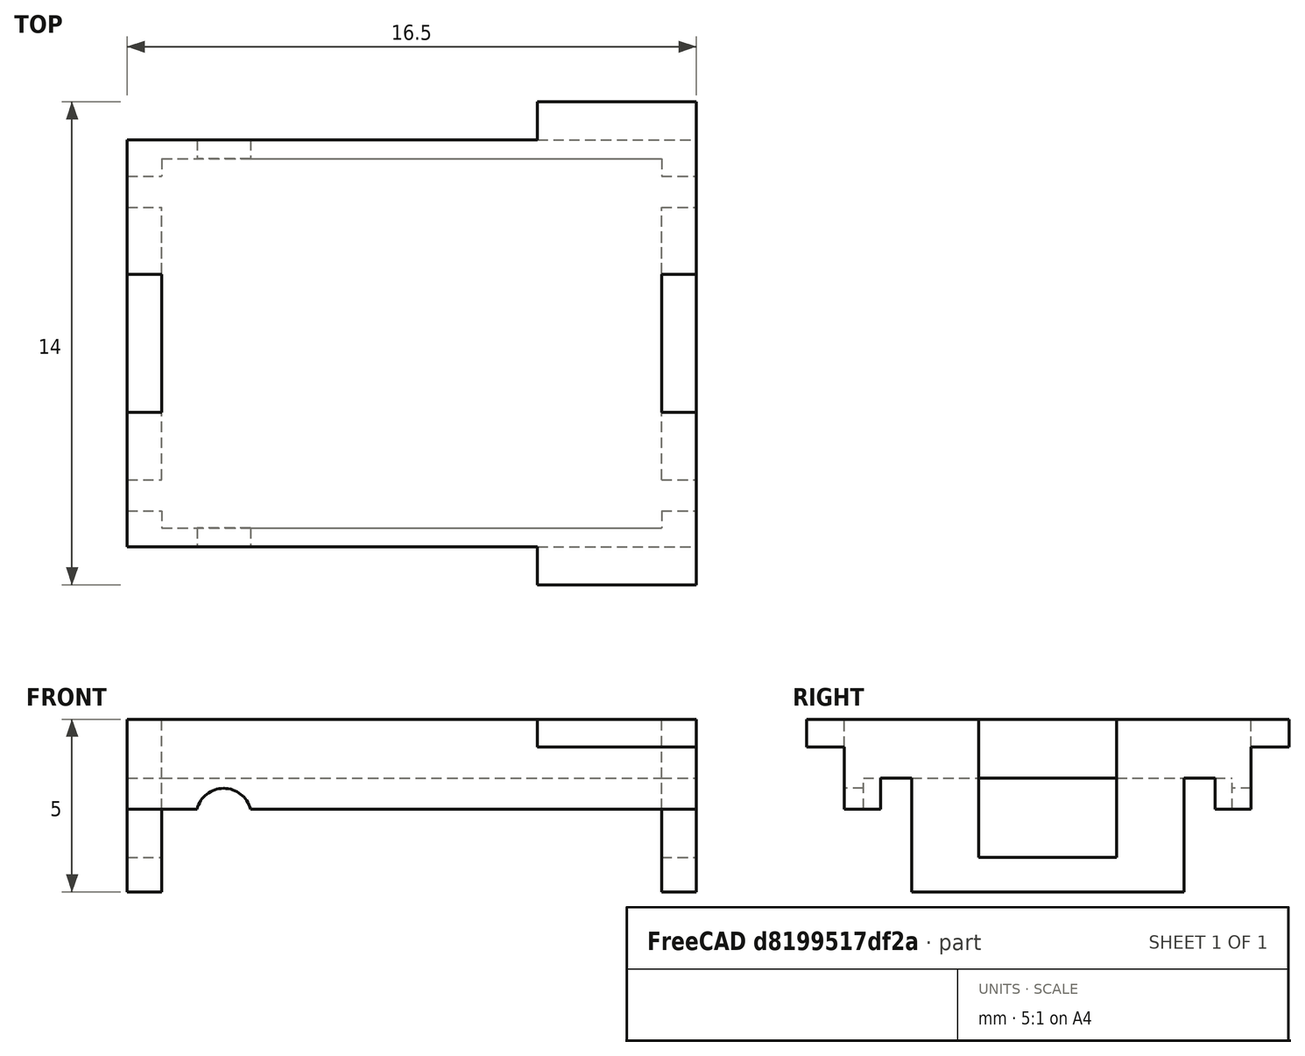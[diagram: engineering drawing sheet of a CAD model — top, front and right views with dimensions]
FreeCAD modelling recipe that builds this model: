
FCSTD DOCUMENT  (FreeCAD 0.18R4 (GitTag))
Label: top
License: All rights reserved
LicenseURL: http://en.wikipedia.org/wiki/All_rights_reserved
objects: Part::Box×12, Part::Cut×9, Part::Compound×3, Part::Cylinder×1
note: 25 computed .brp shape members not serialized (recipe doc carries the construction recipe); baked Part::Feature solids carry a one-line shape summary decoded from their .brp

FEATURE [Part::Box] Box  label="Cube"
  AttacherType = Attacher::AttachEngine3D
  Height = 5
  Length = 16.5
  Placement = pos=(0,-7,0) rot=(0,0,1;0rad)
  Width = 14
FEATURE [Part::Box] Box001  label="Cube001"
  AttacherType = Attacher::AttachEngine3D
  Height = 4
  Length = 1
  Placement = pos=(15.5,-2,1) rot=(0,0,1;0rad)
  Width = 4
  expr: Placement.Base.y = -Width / 2
FEATURE [Part::Box] Box002  label="Cube002"
  AttacherType = Attacher::AttachEngine3D
  Height = 4
  Length = 1
  Placement = pos=(0,-2,1) rot=(0,0,1;0rad)
  Width = 4
  expr: Placement.Base.y = -Width / 2
FEATURE [Part::Box] Box003  label="Cube003"
  AttacherType = Attacher::AttachEngine3D
  Height = 5
  Length = 11.9
  Placement = pos=(0,-7,0) rot=(0,0,1;0rad)
  Width = 1.1
  expr: Length = 16.5 - 4.6
FEATURE [Part::Box] Box004  label="Cube004"
  AttacherType = Attacher::AttachEngine3D
  Height = 5
  Length = 11.9
  Placement = pos=(0,5.9,0) rot=(0,0,1;0rad)
  Width = 1.1
  expr: Length = 16.5 - 4.6
FEATURE [Part::Box] Box005  label="Cube005"
  AttacherType = Attacher::AttachEngine3D
  Height = 4.2
  Length = 4.6
  Placement = pos=(11.9,-7,0) rot=(0,0,1;0rad)
  Width = 1.1
  expr: Length = 4.6
FEATURE [Part::Box] Box006  label="Cube006"
  AttacherType = Attacher::AttachEngine3D
  Height = 4.2
  Length = 4.6
  Placement = pos=(11.9,5.9,0) rot=(0,0,1;0rad)
  Width = 1.1
  expr: Length = 4.6
FEATURE [Part::Box] Box007  label="Cube007"
  AttacherType = Attacher::AttachEngine3D
  Height = 3.3
  Length = 14.5
  Placement = pos=(1,-5.35,0) rot=(0,0,1;0rad)
  Width = 10.7
  expr: Placement.Base.y = -Width / 2
FEATURE [Part::Compound] Compound
  Links = -> [Box001,Box002]
FEATURE [Part::Cut] Cut
  Base = -> Box
  Tool = -> Compound
FEATURE [Part::Cut] Cut001
  Base = -> Cut
  Tool = -> Box006
FEATURE [Part::Cut] Cut002
  Base = -> Cut001
  Tool = -> Box005
FEATURE [Part::Cut] Cut003
  Base = -> Cut002
  Tool = -> Box003
FEATURE [Part::Cut] Cut004
  Base = -> Cut003
  Tool = -> Box004
FEATURE [Part::Cut] Cut005
  Base = -> Cut004
  Tool = -> Box007
FEATURE [Part::Box] Box008  label="Cube008"
  AttacherType = Attacher::AttachEngine3D
  Height = 2.4
  Length = 16.5
  Placement = pos=(0,-5.95,0) rot=(0,0,1;0rad)
  Width = 2
FEATURE [Part::Box] Box009  label="Cube009"
  AttacherType = Attacher::AttachEngine3D
  Height = 2.4
  Length = 16.5
  Placement = pos=(0,3.95,0) rot=(0,0,1;0rad)
  Width = 2
FEATURE [Part::Compound] Compound001
  Links = -> [Box009,Box008]
FEATURE [Part::Cut] Cut006
  Base = -> Cut005
  Tool = -> Compound001
FEATURE [Part::Box] Box010  label="Cube010"
  AttacherType = Attacher::AttachEngine3D
  Height = 0.9
  Length = 16.5
  Placement = pos=(0,3.95,2.4) rot=(0,0,1;0rad)
  Width = 0.9
  expr: Height = 0.9
FEATURE [Part::Box] Box011  label="Cube011"
  AttacherType = Attacher::AttachEngine3D
  Height = 0.9
  Length = 16.5
  Placement = pos=(0,-4.85,2.4) rot=(0,0,1;0rad)
  Width = 0.9
  expr: Height = 0.9
FEATURE [Part::Compound] Compound002
  Links = -> [Box011,Box010]
FEATURE [Part::Cut] Cut007
  Base = -> Cut006
  Tool = -> Compound002
FEATURE [Part::Cylinder] Cylinder
  Angle = 360
  AttacherType = Attacher::AttachEngine3D
  Height = 20
  Placement = pos=(2.8,10,2.2) rot=(1,0,0;1.5708rad)
  Radius = 0.8
FEATURE [Part::Cut] Cut008
  Base = -> Cut007
  Tool = -> Cylinder
